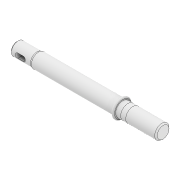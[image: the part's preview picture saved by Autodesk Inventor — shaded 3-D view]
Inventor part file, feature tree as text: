
AUTODESK INVENTOR PART (.ipt)
format: ipt  version: 2022 (Build 260153000, 153)  size: 184,320 bytes
history: native  units: mm
features: extrude x5, sketch x5, plane x2, fillet x2, projected_geometry x2, other x2, loft x1, chamfer x1
ambient origin geometry x8: Origin, YZ Plane, XZ Plane, XY Plane, X Axis, Y Axis, Z Axis, Center Point
bodies: Solid1 (feature_tree)
feature tree (20):
  extrude  "Shaft"  Depth=2.35mm TaperAngle=0.0deg
  extrude  "Slot for Differential Gear"  Depth=2.0mm
  plane  "Work Plane1"
  extrude  "Wheel Insert Profile"  Depth=7.0mm
  loft  "Loft1"
  plane  "Work Plane2"
  extrude  "Stopper"  Depth=7.5mm
  fillet  "Fillet1"  Radius=1.0mm
  extrude  "Differential Gear Insert Profile"  Depth=0.5mm
  fillet  "Fillet3"  Radius=3.0mm
  chamfer  "Chamfer4"  Distance=2.5mm
  sketch  "Sketch1"  dims[d2=0.0mm d9=2.35mm d10=0.0mm]
  sketch  "Sketch2"  dims[d17=1.8mm d20=2.0mm]
  sketch  "Sketch3"  dims[d21=1.0mm d22=7.0mm]
  sketch  "Sketch4"  dims[d25=12.0mm d26=0.0mm d29=2.0mm d32=0.0mm d33=90.0deg]
  projected_geometry  "Projected Loop1"
  other  "Edges2"
  other  "Edges4"
  sketch  "Sketch8"  dims[d34=-41.0mm d35=7.5mm d36=1.0mm d37=0.0mm d38=0.5mm d49=3.0mm d50=2.5mm d62=0.0mm d63=90.0deg d68=5.4mm d69=0.05mm d70=8.0mm d71=0.0mm d72=1.0mm d73=0.5mm d74=2.0mm d75=45.0deg]
  projected_geometry  "Project Cut Edges1"
